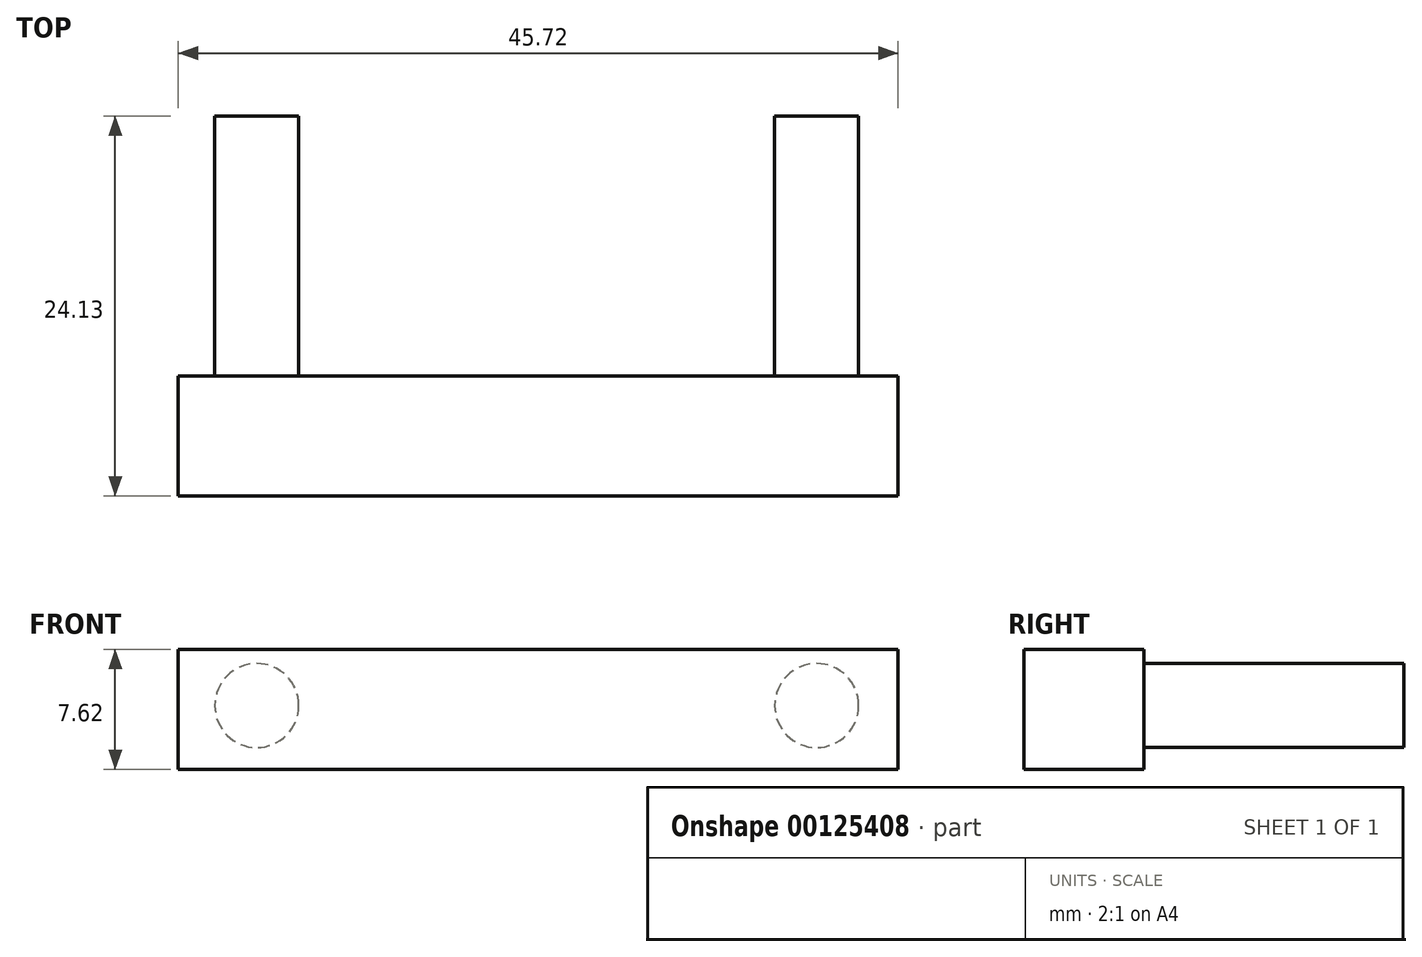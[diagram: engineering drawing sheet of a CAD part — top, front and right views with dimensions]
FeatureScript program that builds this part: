
annotation { "Feature Type Name" : "Feature", "Feature Type Description" : "" }
export const myFeature = defineFeature(function(context is Context, id is Id, definition is map)
    precondition{}
    {
        {
            var Q0;
            Q0=qCreatedBy(makeId("Front.planeOp"),FACE);
            var sketch = newSketch(context, id + "F0", { "sketchPlane" : qUnion([Q0])});
            skLineSegment(sketch, "E0.bottom", {"start": v(-25.43, 3.82) * mm, "end": v(20.29, 3.82) * mm});
            skLineSegment(sketch, "E0.top", {"start": v(-25.43, -3.8) * mm, "end": v(20.29, -3.8) * mm});
            skLineSegment(sketch, "E0.left", {"start": v(-25.43, 3.82) * mm, "end": v(-25.43, -3.8) * mm});
            skLineSegment(sketch, "E0.right", {"start": v(20.29, 3.82) * mm, "end": v(20.29, -3.8) * mm});
            skSolve(sketch);
        }
        {
            var Q0;
            Q0 = qSketchRegion(id + "F0", true);
            extrude(context, id + "F1", {"entities" : qUnion([Q0]), "depth" : 7.62 * mm});
        }
        {
            var Q0;
            Q0=makeQuery(id+"F1.opExtrude","CAP_FACE",FACE,{"disambiguationData":[OSD([sQuery(id+"F0.wireOp",EDGE,"E0.bottom"),sQuery(id+"F0.wireOp",EDGE,"E0.top"),sQuery(id+"F0.wireOp",EDGE,"E0.left"),sQuery(id+"F0.wireOp",EDGE,"E0.right")])],"isStart":false});
            var sketch = newSketch(context, id + "F2", { "sketchPlane" : qUnion([Q0])});
            skLineSegment(sketch, "E1", {"start": v(-20.44, 0.26) * mm, "end": v(15.12, 0.26) * mm, "construction": true});
            skCircle(sketch, "E2", {"center": v(-20.44, 0.26) * mm, "radius": 2.67 * mm});
            skCircle(sketch, "E3", {"center": v(15.12, 0.26) * mm, "radius": 2.67 * mm});
            skSolve(sketch);
        }
        {
            var Q0;
            Q0 = qSketchRegion(id + "F2", true);
            extrude(context, id + "F3", {"entities" : qUnion([Q0]), "operationType" : NewBodyOperationType.ADD, "oppositeDirection" : true, "depth" : 24.13 * mm});
        }
    });
